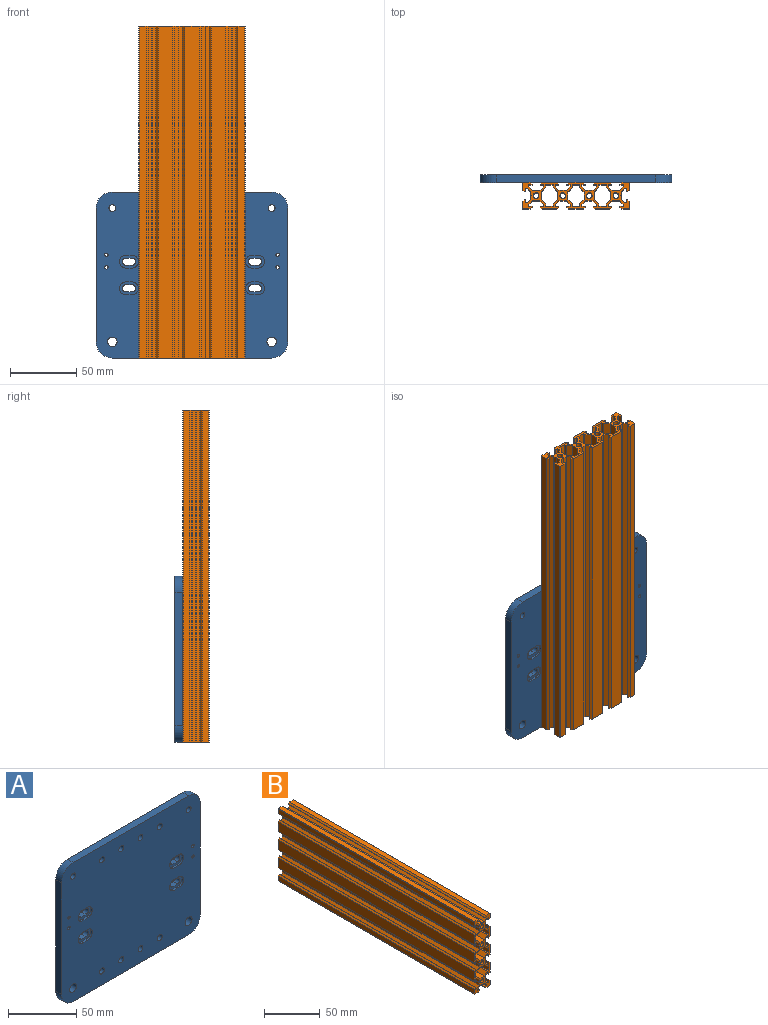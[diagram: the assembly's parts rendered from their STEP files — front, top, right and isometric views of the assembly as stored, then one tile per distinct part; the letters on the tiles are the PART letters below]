
ASSEMBLY  parts=2 mates=1
PART A: 62 faces, bbox 144.4x6x125 mm
  f0: plane 144.4x125mm, normal (0,1,0), area 17433.2mm2, adj f2,f3,f4,f5,f6,f7,f8,f9
  f1: plane 144.4x125mm, normal (0,-1,0), area 17143.4mm2, adj f2,f3,f4,f5,f6,f7,f8,f9
  f2: plane 120x6mm, normal (0,0,-1), area 720mm2, adj f0,f1,f3,f13
  f3: cylinder r=12.2mm len=12.2mm, axis (0,1,0), area 115mm2, adj f0,f1,f2,f4
  f4: plane 100.6x6mm, normal (1,0,0), area 603.6mm2, adj f0,f1,f3,f5
  f5: cylinder r=12.2mm len=12.2mm, axis (0,1,0), area 115mm2, adj f0,f1,f4,f6
  f6: plane 120x6mm, normal (0,0,1), area 720mm2, adj f0,f1,f5,f7
  f7: cylinder r=12.2mm len=12.2mm, axis (0,1,0), area 115mm2, adj f0,f1,f6,f8
  f8: plane 100.6x6mm, normal (-1,0,0), area 603.6mm2, adj f0,f1,f7,f13
  f9: cylinder r=2.55mm len=6mm, axis (0,1,0), area 96.1mm2, adj f0,f1
  f10: cylinder r=2.55mm len=6mm, axis (0,1,0), area 96.1mm2, adj f0,f1
  f11: cylinder r=3.6mm len=7.2mm, axis (0,1,0), area 135.7mm2, adj f0,f1
  f12: cylinder r=3.6mm len=7.2mm, axis (0,1,0), area 135.7mm2, adj f0,f1
  f13: cylinder r=12.2mm len=12.2mm, axis (0,1,0), area 115mm2, adj f0,f1,f2,f8
  f14: cylinder r=2.55mm len=6mm, axis (0,-1,0), area 96.1mm2, adj f0,f1
  f15: cylinder r=2.55mm len=6mm, axis (0,-1,0), area 96.1mm2, adj f0,f1
  f16: cylinder r=2.55mm len=6mm, axis (0,-1,0), area 96.1mm2, adj f0,f1
  f17: cylinder r=2.55mm len=6mm, axis (0,-1,0), area 96.1mm2, adj f0,f1
  f18: cylinder r=2.55mm len=6mm, axis (0,-1,0), area 96.1mm2, adj f0,f1
  f19: cylinder r=2.55mm len=6mm, axis (0,-1,0), area 96.1mm2, adj f0,f1
  f20: cylinder r=2.55mm len=6mm, axis (0,-1,0), area 96.1mm2, adj f0,f1
  f21: cylinder r=2.55mm len=6mm, axis (0,-1,0), area 96.1mm2, adj f0,f1
  f22: plane 5x1.6mm, normal (0,0,-1), area 8mm2, adj f1,f23,f25,f26
  f23: cylinder r=4.75mm len=9.5mm, axis (0,-1,0), area 23.9mm2, adj f1,f22,f24,f26
  f24: plane 5x1.6mm, normal (0,0,1), area 8mm2, adj f1,f23,f25,f26
  f25: cylinder r=4.75mm len=9.5mm, axis (0,-1,0), area 23.9mm2, adj f1,f22,f24,f26
  f26: plane 14.5x9.5mm, normal (0,-1,0), area 72.5mm2, adj f22,f23,f24,f25,f36,f37,f38,f39
  f27: plane 5x1.6mm, normal (0,0,-1), area 8mm2, adj f1,f28,f30,f31
  f28: cylinder r=4.75mm len=9.5mm, axis (0,-1,0), area 23.9mm2, adj f1,f27,f29,f31
  f29: plane 5x1.6mm, normal (0,0,1), area 8mm2, adj f1,f28,f30,f31
  f30: cylinder r=4.75mm len=9.5mm, axis (0,-1,0), area 23.9mm2, adj f1,f27,f29,f31
  f31: plane 14.5x9.5mm, normal (0,-1,0), area 72.5mm2, adj f27,f28,f29,f30,f32,f33,f34,f35
  f32: cylinder r=2.55mm len=5.1mm, axis (0,-1,0), area 35.2mm2, adj f0,f31,f33,f35
  f33: plane 5x4.4mm, normal (0,0,1), area 22mm2, adj f0,f31,f32,f34
  f34: cylinder r=2.55mm len=5.1mm, axis (0,-1,0), area 35.2mm2, adj f0,f31,f33,f35
  f35: plane 5x4.4mm, normal (0,0,-1), area 22mm2, adj f0,f31,f32,f34
  f36: cylinder r=2.55mm len=5.1mm, axis (0,-1,0), area 35.2mm2, adj f0,f26,f37,f39
  f37: plane 5x4.4mm, normal (0,0,1), area 22mm2, adj f0,f26,f36,f38
  f38: cylinder r=2.55mm len=5.1mm, axis (0,-1,0), area 35.2mm2, adj f0,f26,f37,f39
  f39: plane 5x4.4mm, normal (0,0,-1), area 22mm2, adj f0,f26,f36,f38
  f40: cylinder r=1.25mm len=6mm, axis (0,-1,0), area 47.1mm2, adj f0,f1
  f41: cylinder r=1.25mm len=6mm, axis (0,-1,0), area 47.1mm2, adj f0,f1
  f42: plane 5x1.6mm, normal (0,0,-1), area 8mm2, adj f1,f43,f45,f46
  f43: cylinder r=4.75mm len=9.5mm, axis (0,-1,0), area 23.9mm2, adj f1,f42,f44,f46
  f44: plane 5x1.6mm, normal (0,0,1), area 8mm2, adj f1,f43,f45,f46
  f45: cylinder r=4.75mm len=9.5mm, axis (0,-1,0), area 23.9mm2, adj f1,f42,f44,f46
  f46: plane 14.5x9.5mm, normal (0,-1,0), area 72.5mm2, adj f42,f43,f44,f45,f56,f57,f58,f59
  f47: plane 5x1.6mm, normal (0,0,-1), area 8mm2, adj f1,f48,f50,f51
  f48: cylinder r=4.75mm len=9.5mm, axis (0,-1,0), area 23.9mm2, adj f1,f47,f49,f51
  f49: plane 5x1.6mm, normal (0,0,1), area 8mm2, adj f1,f48,f50,f51
  f50: cylinder r=4.75mm len=9.5mm, axis (0,-1,0), area 23.9mm2, adj f1,f47,f49,f51
  f51: plane 14.5x9.5mm, normal (0,-1,0), area 72.5mm2, adj f47,f48,f49,f50,f52,f53,f54,f55
  f52: plane 5x4.4mm, normal (0,0,1), area 22mm2, adj f0,f51,f53,f55
  f53: cylinder r=2.55mm len=5.1mm, axis (0,-1,0), area 35.2mm2, adj f0,f51,f52,f54
  f54: plane 5x4.4mm, normal (0,0,-1), area 22mm2, adj f0,f51,f53,f55
  f55: cylinder r=2.55mm len=5.1mm, axis (0,-1,0), area 35.2mm2, adj f0,f51,f52,f54
  f56: plane 5x4.4mm, normal (0,0,1), area 22mm2, adj f0,f46,f57,f59
  f57: cylinder r=2.55mm len=5.1mm, axis (0,-1,0), area 35.2mm2, adj f0,f46,f56,f58
  f58: plane 5x4.4mm, normal (0,0,-1), area 22mm2, adj f0,f46,f57,f59
  f59: cylinder r=2.55mm len=5.1mm, axis (0,-1,0), area 35.2mm2, adj f0,f46,f56,f58
  f60: cylinder r=1.25mm len=6mm, axis (0,-1,0), area 47.1mm2, adj f0,f1
  f61: cylinder r=1.25mm len=6mm, axis (0,-1,0), area 47.1mm2, adj f0,f1
PART B: 200 faces, bbox 20x250x80 mm
  f0: plane 250x0.35mm, normal (0,0,-1), area 86.2mm2, adj f1,f63,f198,f199
  f1: plane 250x1.46mm, normal (0.71,0,-0.71), area 514.4mm2, adj f0,f2,f198,f199
  f2: plane 250x4.92mm, normal (1,0,0), area 1230mm2, adj f1,f195,f198,f199
  f3: plane 250x4.92mm, normal (0,0,1), area 1230mm2, adj f4,f195,f198,f199
  f4: plane 250x1.46mm, normal (-0.71,0,0.71), area 514.4mm2, adj f3,f5,f198,f199
  f5: plane 250x0.35mm, normal (-1,0,0), area 86.3mm2, adj f4,f64,f198,f199
  f6: plane 250x0.35mm, normal (1,0,0), area 86.3mm2, adj f7,f73,f198,f199
  f7: plane 250x1.46mm, normal (0.71,0,0.71), area 514.4mm2, adj f6,f8,f198,f199
  f8: plane 250x4.92mm, normal (0,0,1), area 1230mm2, adj f7,f196,f198,f199
  f9: plane 250x4.92mm, normal (-1,0,0), area 1230mm2, adj f10,f196,f198,f199
  f10: plane 250x1.46mm, normal (-0.71,0,-0.71), area 514.4mm2, adj f9,f11,f198,f199
  f11: plane 250x0.35mm, normal (0,0,-1), area 86.2mm2, adj f10,f74,f198,f199
  f12: plane 250x0.35mm, normal (0,0,1), area 86.2mm2, adj f13,f83,f198,f199
  f13: plane 250x1.46mm, normal (-0.71,0,0.71), area 514.4mm2, adj f12,f14,f198,f199
  f14: plane 250x10.84mm, normal (-1,0,0), area 2710mm2, adj f13,f15,f198,f199
  f15: plane 250x1.46mm, normal (-0.71,0,-0.71), area 514.4mm2, adj f14,f16,f198,f199
  f16: plane 250x0.35mm, normal (0,0,-1), area 86.2mm2, adj f15,f84,f198,f199
  f17: plane 250x0.35mm, normal (0,0,1), area 86.2mm2, adj f18,f93,f198,f199
  f18: plane 250x1.46mm, normal (-0.71,0,0.71), area 514.4mm2, adj f17,f19,f198,f199
  f19: plane 250x10.84mm, normal (-1,0,0), area 2710mm2, adj f18,f20,f198,f199
  f20: plane 250x1.46mm, normal (-0.71,0,-0.71), area 514.4mm2, adj f19,f21,f198,f199
  f21: plane 250x0.35mm, normal (0,0,-1), area 86.2mm2, adj f20,f94,f198,f199
  f22: plane 250x0.35mm, normal (0,0,1), area 86.2mm2, adj f23,f103,f198,f199
  f23: plane 250x1.46mm, normal (-0.71,0,0.71), area 514.4mm2, adj f22,f24,f198,f199
  f24: plane 250x10.84mm, normal (-1,0,0), area 2710mm2, adj f23,f25,f198,f199
  f25: plane 250x1.46mm, normal (-0.71,0,-0.71), area 514.4mm2, adj f24,f26,f198,f199
  f26: plane 250x0.35mm, normal (0,0,-1), area 86.2mm2, adj f25,f104,f198,f199
  f27: plane 250x0.35mm, normal (0,0,1), area 86.2mm2, adj f28,f113,f198,f199
  f28: plane 250x1.46mm, normal (-0.71,0,0.71), area 514.4mm2, adj f27,f29,f198,f199
  f29: plane 250x4.92mm, normal (-1,0,0), area 1230mm2, adj f28,f114,f198,f199
  f30: plane 250x4.92mm, normal (0,0,-1), area 1230mm2, adj f31,f114,f198,f199
  f31: plane 250x1.46mm, normal (0.71,0,-0.71), area 514.4mm2, adj f30,f32,f198,f199
  f32: plane 250x0.35mm, normal (1,0,0), area 86.3mm2, adj f31,f115,f198,f199
  f33: plane 250x0.35mm, normal (-1,0,0), area 86.3mm2, adj f34,f124,f198,f199
  f34: plane 250x1.46mm, normal (-0.71,0,-0.71), area 514.4mm2, adj f33,f35,f198,f199
  f35: plane 250x4.92mm, normal (0,0,-1), area 1230mm2, adj f34,f197,f198,f199
  f36: plane 250x4.92mm, normal (1,0,0), area 1230mm2, adj f37,f197,f198,f199
  f37: plane 250x1.46mm, normal (0.71,0,0.71), area 514.4mm2, adj f36,f38,f198,f199
  f38: plane 250x0.35mm, normal (0,0,1), area 86.2mm2, adj f37,f125,f198,f199
  f39: plane 250x0.35mm, normal (0,0,-1), area 86.2mm2, adj f40,f134,f198,f199
  f40: plane 250x1.46mm, normal (0.71,0,-0.71), area 514.4mm2, adj f39,f41,f198,f199
  f41: plane 250x10.84mm, normal (1,0,0), area 2710mm2, adj f40,f42,f198,f199
  f42: plane 250x1.46mm, normal (0.71,0,0.71), area 514.4mm2, adj f41,f43,f198,f199
  f43: plane 250x0.35mm, normal (0,0,1), area 86.2mm2, adj f42,f135,f198,f199
  f44: plane 250x0.35mm, normal (0,0,-1), area 86.2mm2, adj f45,f144,f198,f199
  f45: plane 250x1.46mm, normal (0.71,0,-0.71), area 514.4mm2, adj f44,f46,f198,f199
  f46: plane 250x10.84mm, normal (1,0,0), area 2710mm2, adj f45,f47,f198,f199
  f47: plane 250x1.46mm, normal (0.71,0,0.71), area 514.4mm2, adj f46,f48,f198,f199
  f48: plane 250x0.35mm, normal (0,0,1), area 86.2mm2, adj f47,f145,f198,f199
  f49: plane 250x0.35mm, normal (0,0,-1), area 86.2mm2, adj f50,f154,f198,f199
  f50: plane 250x1.46mm, normal (0.71,0,-0.71), area 514.4mm2, adj f49,f51,f198,f199
  f51: plane 250x10.84mm, normal (1,0,0), area 2710mm2, adj f50,f52,f198,f199
  f52: plane 250x1.46mm, normal (0.71,0,0.71), area 514.4mm2, adj f51,f53,f198,f199
  f53: plane 250x0.35mm, normal (0,0,1), area 86.2mm2, adj f52,f155,f198,f199
  f54: cylinder r=2.1mm len=250mm, axis (0,1,0), area 3298.7mm2, adj f198,f199
  f55: cylinder r=2.1mm len=250mm, axis (0,1,0), area 3298.7mm2, adj f198,f199
  f56: cylinder r=2.1mm len=250mm, axis (0,1,0), area 3298.7mm2, adj f198,f199
  f57: cylinder r=2.1mm len=250mm, axis (0,1,0), area 3298.7mm2, adj f198,f199
  f58: plane 250x0.21mm, normal (0.71,0,0.71), area 74.2mm2, adj f59,f191,f198,f199
  f59: plane 250x0.21mm, normal (0.71,0,-0.71), area 74.2mm2, adj f58,f60,f198,f199
  f60: plane 250x2.63mm, normal (1,0,0), area 657.3mm2, adj f59,f61,f198,f199
  f61: plane 250x2.66mm, normal (0.71,0,-0.71), area 940.7mm2, adj f60,f62,f198,f199
  f62: plane 250x1.64mm, normal (0,0,-1), area 409.8mm2, adj f61,f63,f198,f199
  f63: plane 250x2.38mm, normal (-1,0,0), area 593.7mm2, adj f0,f62,f198,f199
  f64: plane 250x2.38mm, normal (0,0,-1), area 593.7mm2, adj f5,f65,f198,f199
  f65: plane 250x1.64mm, normal (-1,0,0), area 409.8mm2, adj f64,f66,f198,f199
  f66: plane 250x2.66mm, normal (-0.71,0,0.71), area 940.7mm2, adj f65,f67,f198,f199
  f67: plane 250x2.63mm, normal (0,0,1), area 657.3mm2, adj f66,f68,f198,f199
  f68: plane 250x0.21mm, normal (-0.71,0,0.71), area 74.2mm2, adj f67,f69,f198,f199
  f69: plane 250x0.21mm, normal (0.71,0,0.71), area 74.2mm2, adj f68,f70,f198,f199
  f70: plane 250x2.63mm, normal (0,0,1), area 657.3mm2, adj f69,f71,f198,f199
  f71: plane 250x2.66mm, normal (0.71,0,0.71), area 940.7mm2, adj f70,f72,f198,f199
  f72: plane 250x1.64mm, normal (1,0,0), area 409.8mm2, adj f71,f73,f198,f199
  f73: plane 250x2.38mm, normal (0,0,-1), area 593.7mm2, adj f6,f72,f198,f199
  f74: plane 250x2.38mm, normal (1,0,0), area 593.7mm2, adj f11,f75,f198,f199
  f75: plane 250x1.64mm, normal (0,0,-1), area 409.8mm2, adj f74,f76,f198,f199
  f76: plane 250x2.66mm, normal (-0.71,0,-0.71), area 940.7mm2, adj f75,f77,f198,f199
  f77: plane 250x2.63mm, normal (-1,0,0), area 657.3mm2, adj f76,f78,f198,f199
  f78: plane 250x0.21mm, normal (-0.71,0,-0.71), area 74.2mm2, adj f77,f79,f198,f199
  f79: plane 250x0.21mm, normal (-0.71,0,0.71), area 74.2mm2, adj f78,f80,f198,f199
  f80: plane 250x2.63mm, normal (-1,0,0), area 657.3mm2, adj f79,f81,f198,f199
  f81: plane 250x2.66mm, normal (-0.71,0,0.71), area 940.7mm2, adj f80,f82,f198,f199
  f82: plane 250x1.64mm, normal (0,0,1), area 409.8mm2, adj f81,f83,f198,f199
  f83: plane 250x2.38mm, normal (1,0,0), area 593.7mm2, adj f12,f82,f198,f199
  f84: plane 250x2.38mm, normal (1,0,0), area 593.8mm2, adj f16,f85,f198,f199
  f85: plane 250x1.64mm, normal (0,0,-1), area 409.8mm2, adj f84,f86,f198,f199
  f86: plane 250x2.66mm, normal (-0.71,0,-0.71), area 940.7mm2, adj f85,f87,f198,f199
  f87: plane 250x2.63mm, normal (-1,0,0), area 657.3mm2, adj f86,f88,f198,f199
  f88: plane 250x0.21mm, normal (-0.71,0,-0.71), area 74.2mm2, adj f87,f89,f198,f199
  f89: plane 250x0.21mm, normal (-0.71,0,0.71), area 74.2mm2, adj f88,f90,f198,f199
  f90: plane 250x2.63mm, normal (-1,0,0), area 657.3mm2, adj f89,f91,f198,f199
  f91: plane 250x2.66mm, normal (-0.71,0,0.71), area 940.7mm2, adj f90,f92,f198,f199
  f92: plane 250x1.64mm, normal (0,0,1), area 409.8mm2, adj f91,f93,f198,f199
  f93: plane 250x2.38mm, normal (1,0,0), area 593.8mm2, adj f17,f92,f198,f199
  f94: plane 250x2.38mm, normal (1,0,0), area 593.8mm2, adj f21,f95,f198,f199
  f95: plane 250x1.64mm, normal (0,0,-1), area 409.8mm2, adj f94,f96,f198,f199
  f96: plane 250x2.66mm, normal (-0.71,0,-0.71), area 940.7mm2, adj f95,f97,f198,f199
  f97: plane 250x2.63mm, normal (-1,0,0), area 657.3mm2, adj f96,f98,f198,f199
  f98: plane 250x0.21mm, normal (-0.71,0,-0.71), area 74.2mm2, adj f97,f99,f198,f199
  f99: plane 250x0.21mm, normal (-0.71,0,0.71), area 74.2mm2, adj f98,f100,f198,f199
  f100: plane 250x2.63mm, normal (-1,0,0), area 657.3mm2, adj f99,f101,f198,f199
  f101: plane 250x2.66mm, normal (-0.71,0,0.71), area 940.7mm2, adj f100,f102,f198,f199
  f102: plane 250x1.64mm, normal (0,0,1), area 409.8mm2, adj f101,f103,f198,f199
  f103: plane 250x2.38mm, normal (1,0,0), area 593.8mm2, adj f22,f102,f198,f199
  f104: plane 250x2.38mm, normal (1,0,0), area 593.7mm2, adj f26,f105,f198,f199
  f105: plane 250x1.64mm, normal (0,0,-1), area 409.8mm2, adj f104,f106,f198,f199
  f106: plane 250x2.66mm, normal (-0.71,0,-0.71), area 940.7mm2, adj f105,f107,f198,f199
  f107: plane 250x2.63mm, normal (-1,0,0), area 657.3mm2, adj f106,f108,f198,f199
  f108: plane 250x0.21mm, normal (-0.71,0,-0.71), area 74.2mm2, adj f107,f109,f198,f199
  f109: plane 250x0.21mm, normal (-0.71,0,0.71), area 74.2mm2, adj f108,f110,f198,f199
  f110: plane 250x2.63mm, normal (-1,0,0), area 657.3mm2, adj f109,f111,f198,f199
  f111: plane 250x2.66mm, normal (-0.71,0,0.71), area 940.7mm2, adj f110,f112,f198,f199
  f112: plane 250x1.64mm, normal (0,0,1), area 409.8mm2, adj f111,f113,f198,f199
  f113: plane 250x2.38mm, normal (1,0,0), area 593.7mm2, adj f27,f112,f198,f199
  f114: cylinder r=0.5mm len=250mm, axis (0,1,0), area 196.3mm2, adj f29,f30,f198,f199
  f115: plane 250x2.38mm, normal (0,0,1), area 593.7mm2, adj f32,f116,f198,f199
  f116: plane 250x1.64mm, normal (1,0,0), area 409.8mm2, adj f115,f117,f198,f199
  f117: plane 250x2.66mm, normal (0.71,0,-0.71), area 940.7mm2, adj f116,f118,f198,f199
  f118: plane 250x2.63mm, normal (0,0,-1), area 657.3mm2, adj f117,f119,f198,f199
  f119: plane 250x0.21mm, normal (0.71,0,-0.71), area 74.2mm2, adj f118,f120,f198,f199
  f120: plane 250x0.21mm, normal (-0.71,0,-0.71), area 74.2mm2, adj f119,f121,f198,f199
  f121: plane 250x2.63mm, normal (0,0,-1), area 657.3mm2, adj f120,f122,f198,f199
  f122: plane 250x2.66mm, normal (-0.71,0,-0.71), area 940.7mm2, adj f121,f123,f198,f199
  f123: plane 250x1.64mm, normal (-1,0,0), area 409.8mm2, adj f122,f124,f198,f199
  f124: plane 250x2.38mm, normal (0,0,1), area 593.7mm2, adj f33,f123,f198,f199
  f125: plane 250x2.38mm, normal (-1,0,0), area 593.7mm2, adj f38,f126,f198,f199
  f126: plane 250x1.64mm, normal (0,0,1), area 409.8mm2, adj f125,f127,f198,f199
  f127: plane 250x2.66mm, normal (0.71,0,0.71), area 940.7mm2, adj f126,f128,f198,f199
  f128: plane 250x2.63mm, normal (1,0,0), area 657.3mm2, adj f127,f129,f198,f199
  f129: plane 250x0.21mm, normal (0.71,0,0.71), area 74.2mm2, adj f128,f130,f198,f199
  f130: plane 250x0.21mm, normal (0.71,0,-0.71), area 74.2mm2, adj f129,f131,f198,f199
  f131: plane 250x2.63mm, normal (1,0,0), area 657.3mm2, adj f130,f132,f198,f199
  f132: plane 250x2.66mm, normal (0.71,0,-0.71), area 940.7mm2, adj f131,f133,f198,f199
  f133: plane 250x1.64mm, normal (0,0,-1), area 409.8mm2, adj f132,f134,f198,f199
  f134: plane 250x2.38mm, normal (-1,0,0), area 593.7mm2, adj f39,f133,f198,f199
  f135: plane 250x2.38mm, normal (-1,0,0), area 593.8mm2, adj f43,f136,f198,f199
  f136: plane 250x1.64mm, normal (0,0,1), area 409.8mm2, adj f135,f137,f198,f199
  f137: plane 250x2.66mm, normal (0.71,0,0.71), area 940.7mm2, adj f136,f138,f198,f199
  f138: plane 250x2.63mm, normal (1,0,0), area 657.3mm2, adj f137,f139,f198,f199
  f139: plane 250x0.21mm, normal (0.71,0,0.71), area 74.2mm2, adj f138,f140,f198,f199
  f140: plane 250x0.21mm, normal (0.71,0,-0.71), area 74.2mm2, adj f139,f141,f198,f199
  f141: plane 250x2.63mm, normal (1,0,0), area 657.3mm2, adj f140,f142,f198,f199
  f142: plane 250x2.66mm, normal (0.71,0,-0.71), area 940.7mm2, adj f141,f143,f198,f199
  f143: plane 250x1.64mm, normal (0,0,-1), area 409.8mm2, adj f142,f144,f198,f199
  f144: plane 250x2.38mm, normal (-1,0,0), area 593.8mm2, adj f44,f143,f198,f199
  f145: plane 250x2.38mm, normal (-1,0,0), area 593.8mm2, adj f48,f146,f198,f199
  f146: plane 250x1.64mm, normal (0,0,1), area 409.8mm2, adj f145,f147,f198,f199
  f147: plane 250x2.66mm, normal (0.71,0,0.71), area 940.7mm2, adj f146,f148,f198,f199
  f148: plane 250x2.63mm, normal (1,0,0), area 657.3mm2, adj f147,f149,f198,f199
  f149: plane 250x0.21mm, normal (0.71,0,0.71), area 74.2mm2, adj f148,f150,f198,f199
  f150: plane 250x0.21mm, normal (0.71,0,-0.71), area 74.2mm2, adj f149,f151,f198,f199
  f151: plane 250x2.63mm, normal (1,0,0), area 657.3mm2, adj f150,f152,f198,f199
  f152: plane 250x2.66mm, normal (0.71,0,-0.71), area 940.7mm2, adj f151,f153,f198,f199
  f153: plane 250x1.64mm, normal (0,0,-1), area 409.8mm2, adj f152,f154,f198,f199
  f154: plane 250x2.38mm, normal (-1,0,0), area 593.8mm2, adj f49,f153,f198,f199
  f155: plane 250x2.38mm, normal (-1,0,0), area 593.7mm2, adj f53,f156,f198,f199
  f156: plane 250x1.64mm, normal (0,0,1), area 409.8mm2, adj f155,f157,f198,f199
  f157: plane 250x2.66mm, normal (0.71,0,0.71), area 940.7mm2, adj f156,f191,f198,f199
  f158: plane 250x1.96mm, normal (0,0,1), area 490.2mm2, adj f159,f192,f198,f199
  f159: plane 250x5.4mm, normal (1,0,0), area 1350mm2, adj f158,f160,f198,f199
  f160: plane 250x1.96mm, normal (0,0,-1), area 490.2mm2, adj f159,f161,f198,f199
  f161: plane 250x3.4mm, normal (0.71,0,-0.71), area 1202.1mm2, adj f160,f162,f198,f199
  f162: plane 250x5.68mm, normal (0,0,-1), area 1419.7mm2, adj f161,f163,f198,f199
  f163: plane 250x3.4mm, normal (-0.71,0,-0.71), area 1202.1mm2, adj f162,f164,f198,f199
  f164: plane 250x1.96mm, normal (0,0,-1), area 490.2mm2, adj f163,f165,f198,f199
  f165: plane 250x5.4mm, normal (-1,0,0), area 1350mm2, adj f164,f166,f198,f199
  f166: plane 250x1.96mm, normal (0,0,1), area 490.2mm2, adj f165,f167,f198,f199
  f167: plane 250x3.4mm, normal (-0.71,0,0.71), area 1202.1mm2, adj f166,f168,f198,f199
  f168: plane 250x5.68mm, normal (0,0,1), area 1419.7mm2, adj f167,f192,f198,f199
  f169: plane 250x1.96mm, normal (0,0,1), area 490.2mm2, adj f170,f193,f198,f199
  f170: plane 250x5.4mm, normal (1,0,0), area 1350mm2, adj f169,f171,f198,f199
  f171: plane 250x1.96mm, normal (0,0,-1), area 490.2mm2, adj f170,f172,f198,f199
  f172: plane 250x3.4mm, normal (0.71,0,-0.71), area 1202.1mm2, adj f171,f173,f198,f199
  f173: plane 250x5.68mm, normal (0,0,-1), area 1419.7mm2, adj f172,f174,f198,f199
  f174: plane 250x3.4mm, normal (-0.71,0,-0.71), area 1202.1mm2, adj f173,f175,f198,f199
  f175: plane 250x1.96mm, normal (0,0,-1), area 490.2mm2, adj f174,f176,f198,f199
  f176: plane 250x5.4mm, normal (-1,0,0), area 1350mm2, adj f175,f177,f198,f199
  f177: plane 250x1.96mm, normal (0,0,1), area 490.2mm2, adj f176,f178,f198,f199
  f178: plane 250x3.4mm, normal (-0.71,0,0.71), area 1202.1mm2, adj f177,f179,f198,f199
  f179: plane 250x5.68mm, normal (0,0,1), area 1419.7mm2, adj f178,f193,f198,f199
  f180: plane 250x1.96mm, normal (0,0,1), area 490.2mm2, adj f181,f194,f198,f199
  f181: plane 250x5.4mm, normal (1,0,0), area 1350mm2, adj f180,f182,f198,f199
  f182: plane 250x1.96mm, normal (0,0,-1), area 490.2mm2, adj f181,f183,f198,f199
  f183: plane 250x3.4mm, normal (0.71,0,-0.71), area 1202.1mm2, adj f182,f184,f198,f199
  f184: plane 250x5.68mm, normal (0,0,-1), area 1419.7mm2, adj f183,f185,f198,f199
  f185: plane 250x3.4mm, normal (-0.71,0,-0.71), area 1202.1mm2, adj f184,f186,f198,f199
  f186: plane 250x1.96mm, normal (0,0,-1), area 490.2mm2, adj f185,f187,f198,f199
  f187: plane 250x5.4mm, normal (-1,0,0), area 1350mm2, adj f186,f188,f198,f199
  f188: plane 250x1.96mm, normal (0,0,1), area 490.2mm2, adj f187,f189,f198,f199
  f189: plane 250x3.4mm, normal (-0.71,0,0.71), area 1202.1mm2, adj f188,f190,f198,f199
  f190: plane 250x5.68mm, normal (0,0,1), area 1419.7mm2, adj f189,f194,f198,f199
  f191: plane 250x2.63mm, normal (1,0,0), area 657.3mm2, adj f58,f157,f198,f199
  f192: plane 250x3.4mm, normal (0.71,0,0.71), area 1202.1mm2, adj f158,f168,f198,f199
  f193: plane 250x3.4mm, normal (0.71,0,0.71), area 1202.1mm2, adj f169,f179,f198,f199
  f194: plane 250x3.4mm, normal (0.71,0,0.71), area 1202.1mm2, adj f180,f190,f198,f199
  f195: cylinder r=0.5mm len=250mm, axis (0,1,0), area 196.3mm2, adj f2,f3,f198,f199
  f196: cylinder r=0.5mm len=250mm, axis (0,1,0), area 196.3mm2, adj f8,f9,f198,f199
  f197: cylinder r=0.5mm len=250mm, axis (0,1,0), area 196.3mm2, adj f35,f36,f198,f199
  f198: plane 80x20mm, normal (0,1,0), area 557.2mm2, adj f0,f1,f2,f3,f4,f5,f6,f7
  f199: plane 80x20mm, normal (0,-1,0), area 557.2mm2, adj f0,f1,f2,f3,f4,f5,f6,f7
PLACE A at identity fixed
PLACE B rot(axis=(-0.58,0.58,-0.58),120deg) t=(0,-16,-62.5)mm
MATE planar A.f1 <-> B.f19  axis (0,-1,0) through (0,-6,-62.5)mm
